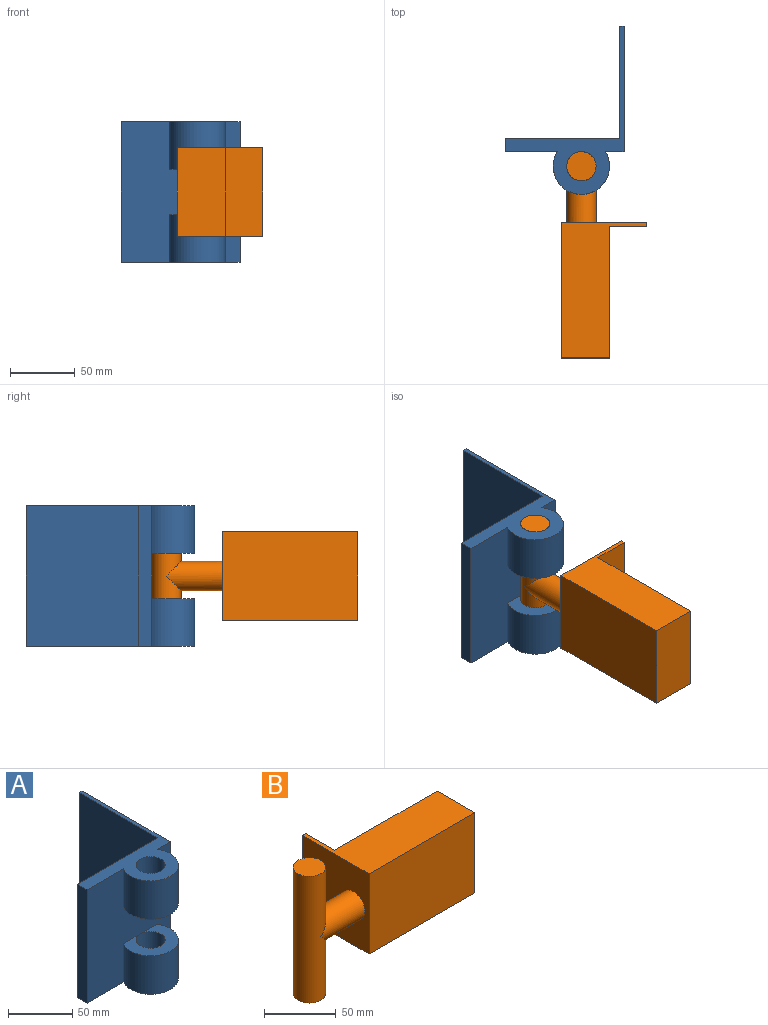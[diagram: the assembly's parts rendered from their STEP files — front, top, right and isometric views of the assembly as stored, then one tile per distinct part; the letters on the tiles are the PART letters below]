
ASSEMBLY  parts=2 mates=1
PART A: 14 faces, bbox 91.6x129.8x108 mm
  f0: cylinder r=21.72mm len=43.43mm, axis (0,0,-1), area 3356.9mm2, adj f3,f11,f13
  f1: cylinder r=11.3mm len=36.49mm, axis (0,0,-1), area 2591.3mm2, adj f11,f13
  f2: cylinder r=21.72mm len=43.43mm, axis (0,0,-1), area 3356.9mm2, adj f3,f10,f12
  f3: plane 107.95x91.57mm, normal (0,-1,0), area 7178.2mm2, adj f0,f2,f4,f8,f10,f11,f12,f13
  f4: plane 107.95x96.77mm, normal (1,0,0), area 10446.8mm2, adj f3,f5,f10,f11
  f5: plane 107.95x3.18mm, normal (0,1,0), area 342.7mm2, adj f4,f6,f10,f11
  f6: plane 107.95x86.36mm, normal (-1,0,0), area 9322.6mm2, adj f5,f7,f10,f11
  f7: plane 107.95x88.39mm, normal (0,1,0), area 9541.9mm2, adj f6,f8,f10,f11
  f8: plane 107.95x10.41mm, normal (-1,0,0), area 1124.2mm2, adj f3,f7,f10,f11
  f9: cylinder r=11.3mm len=36.49mm, axis (0,0,-1), area 2591.3mm2, adj f10,f12
  f10: plane 129.79x91.57mm, normal (0,0,1), area 2035mm2, adj f2,f3,f4,f5,f6,f7,f8,f9
  f11: plane 129.79x91.57mm, normal (0,0,-1), area 2035mm2, adj f0,f1,f3,f4,f5,f6,f7,f8
  f12: plane 43.43x33.02mm, normal (0,0,-1), area 807.2mm2, adj f2,f3,f9
  f13: plane 43.43x33.02mm, normal (0,0,1), area 807.2mm2, adj f0,f1,f3
PART B: 12 faces, bbox 158.9x65.8x108 mm
  f0: cylinder r=11.3mm len=43.43mm, axis (1,0,0), area 2573.6mm2, adj f4,f9
  f1: plane 100.99x68.33mm, normal (0,1,0), area 6900.6mm2, adj f2,f6,f7,f8
  f2: plane 68.33x28.7mm, normal (1,0,0), area 1961.1mm2, adj f1,f3,f7,f8
  f3: plane 68.33x3.18mm, normal (0,1,0), area 216.9mm2, adj f2,f4,f7,f8
  f4: plane 68.33x65.79mm, normal (-1,0,0), area 4093.5mm2, adj f0,f3,f5,f7,f8
  f5: plane 104.17x68.33mm, normal (0,-1,0), area 7117.5mm2, adj f4,f6,f7,f8
  f6: plane 68.33x37.08mm, normal (1,0,0), area 2533.8mm2, adj f1,f5,f7,f8
  f7: plane 104.17x65.79mm, normal (0,0,1), area 3954.2mm2, adj f1,f2,f3,f4,f5,f6
  f8: plane 104.17x65.79mm, normal (0,0,-1), area 3954.2mm2, adj f1,f2,f3,f4,f5,f6
  f9: cylinder r=11.3mm len=107.95mm, axis (0,0,-1), area 7155.5mm2, adj f0,f10,f11
  f10: plane 22.61x22.61mm, normal (0,0,1), area 401.4mm2, adj f9
  f11: plane 22.61x22.61mm, normal (0,0,-1), area 401.4mm2, adj f9
PLACE A t=(-222.87,96.45,29.43)mm fixed
PLACE B rot(axis=(0,0,-1),90deg) t=(-230.87,31.3,29.43)mm
MATE revolute A.f0 <-> B.f9  axis (0,0,-1) through (-252.59,74.73,83.41)mm
